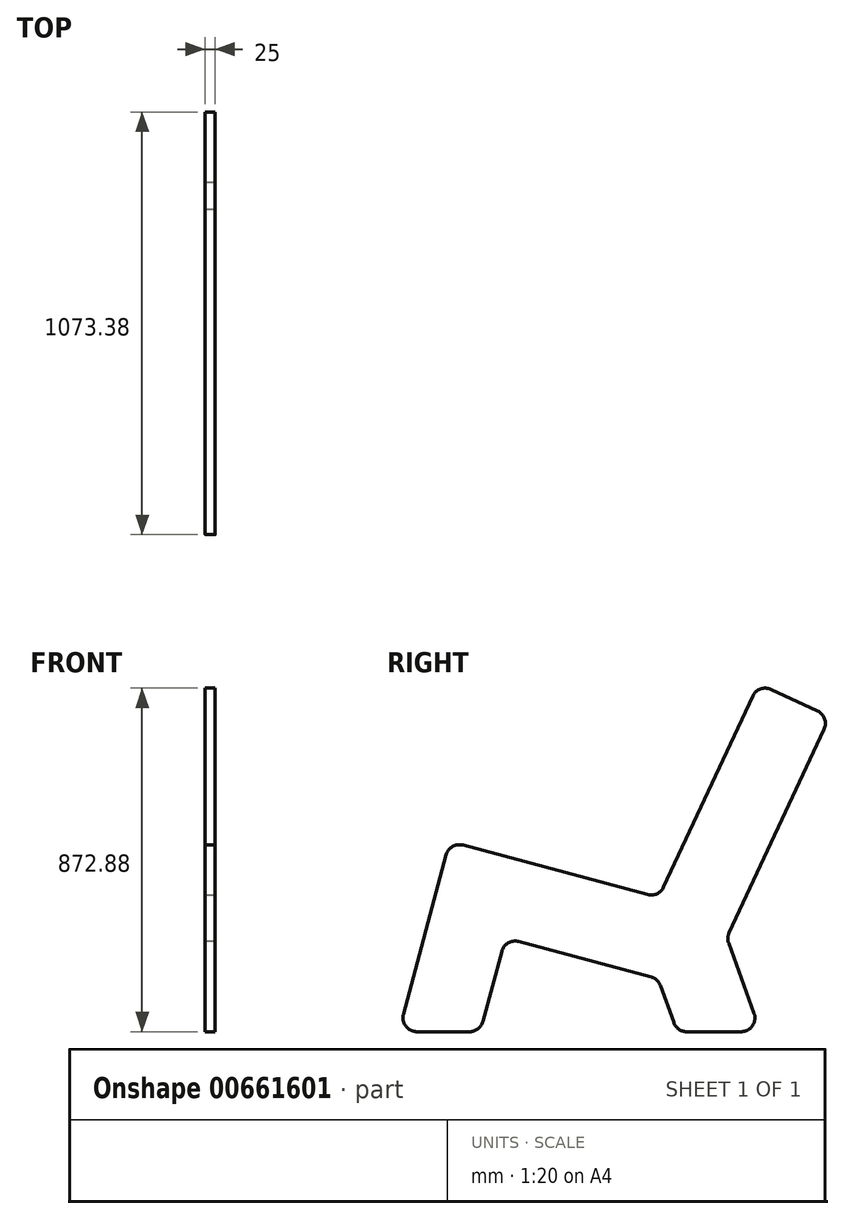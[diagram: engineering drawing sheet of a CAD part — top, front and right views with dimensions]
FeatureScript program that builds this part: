
annotation { "Feature Type Name" : "Feature", "Feature Type Description" : "" }
export const myFeature = defineFeature(function(context is Context, id is Id, definition is map)
    precondition{}
    {
        {
            var Q0;
            Q0=qCreatedBy(makeId("Right.planeOp"),FACE);
            cPlane(context, id + "F0", {"entities" : qUnion([Q0]), "cplaneType" : CPlaneType.OFFSET, "offset" : 400 * mm, "oppositeDirection" : true, "width" : 150 * mm, "height" : 150 * mm});
        }
        {
            var Q0;
            Q0=qCreatedBy(id+"F0.planeOp",FACE);
            var sketch = newSketch(context, id + "F1", { "sketchPlane" : qUnion([Q0])});
            skLineSegment(sketch, "E0", {"start": v(0, 0) * mm, "end": v(129.4, 482.96) * mm});
            skLineSegment(sketch, "E1", {"start": v(129.4, 482.96) * mm, "end": v(660.67, 340.61) * mm});
            skLineSegment(sketch, "E2", {"start": v(660.67, 340.61) * mm, "end": v(914.24, 884.4) * mm});
            skLineSegment(sketch, "E3", {"start": v(914.24, 884.4) * mm, "end": v(1095.5, 799.87) * mm});
            skLineSegment(sketch, "E4", {"start": v(1095.5, 799.87) * mm, "end": v(833.37, 237.72) * mm});
            skLineSegment(sketch, "E5", {"start": v(0, 0) * mm, "end": v(207.06, 0) * mm});
            skLineSegment(sketch, "E6", {"start": v(207.06, 0) * mm, "end": v(270.83, 238.01) * mm});
            skLineSegment(sketch, "E7", {"start": v(270.83, 238.01) * mm, "end": v(658.2, 134.22) * mm});
            skLineSegment(sketch, "E8", {"start": v(658.2, 134.22) * mm, "end": v(707.06, 0) * mm});
            skLineSegment(sketch, "E9", {"start": v(707.06, 0) * mm, "end": v(919.9, 0) * mm});
            skLineSegment(sketch, "E10", {"start": v(919.9, 0) * mm, "end": v(833.37, 237.72) * mm});
            skSolve(sketch);
        }
        {
            var Q0;
            Q0=makeQuery(id+"F1.imprint","IMPRINT",FACE,{"disambiguationData":[TD([[makeQuery(id+"F1.imprint","IMPRINT",EDGE,{"derivedFrom":sQuery(id+"F1.wireOp",EDGE,"E0")}),-1.0]])]});
            extrude(context, id + "F2", {"entities" : qUnion([Q0]), "depth" : 25 * mm, "offsetDistance" : 25 * mm});
        }
        {
            var Q0;
            Q0=makeQuery(id+"F2.opExtrude","SWEPT_EDGE",EDGE,{"disambiguationData":[OSD([sQuery(id+"F1.wireOp",EDGE,"E0"),sQuery(id+"F1.wireOp",EDGE,"E1")])]});
            var Q1;
            Q1=makeQuery(id+"F2.opExtrude","SWEPT_EDGE",EDGE,{"disambiguationData":[OSD([sQuery(id+"F1.wireOp",EDGE,"E1"),sQuery(id+"F1.wireOp",EDGE,"E2")])]});
            var Q2;
            Q2=makeQuery(id+"F2.opExtrude","SWEPT_EDGE",EDGE,{"disambiguationData":[OSD([sQuery(id+"F1.wireOp",EDGE,"E2"),sQuery(id+"F1.wireOp",EDGE,"E3")])]});
            var Q3;
            Q3=makeQuery(id+"F2.opExtrude","SWEPT_EDGE",EDGE,{"disambiguationData":[OSD([sQuery(id+"F1.wireOp",EDGE,"E3"),sQuery(id+"F1.wireOp",EDGE,"E4")])]});
            var Q4;
            Q4=makeQuery(id+"F2.opExtrude","SWEPT_EDGE",EDGE,{"disambiguationData":[OSD([sQuery(id+"F1.wireOp",EDGE,"E6"),sQuery(id+"F1.wireOp",EDGE,"E7")])]});
            var Q5;
            Q5=makeQuery(id+"F2.opExtrude","SWEPT_EDGE",EDGE,{"disambiguationData":[OSD([sQuery(id+"F1.wireOp",EDGE,"E7"),sQuery(id+"F1.wireOp",EDGE,"E8")])]});
            var Q6;
            Q6=makeQuery(id+"F2.opExtrude","SWEPT_EDGE",EDGE,{"disambiguationData":[OSD([sQuery(id+"F1.wireOp",EDGE,"E0"),sQuery(id+"F1.wireOp",EDGE,"E5")])]});
            var Q7;
            Q7=makeQuery(id+"F2.opExtrude","SWEPT_EDGE",EDGE,{"disambiguationData":[OSD([sQuery(id+"F1.wireOp",EDGE,"E5"),sQuery(id+"F1.wireOp",EDGE,"E6")])]});
            var Q8;
            Q8=makeQuery(id+"F2.opExtrude","SWEPT_EDGE",EDGE,{"disambiguationData":[OSD([sQuery(id+"F1.wireOp",EDGE,"E8"),sQuery(id+"F1.wireOp",EDGE,"E9")])]});
            var Q9;
            Q9=makeQuery(id+"F2.opExtrude","SWEPT_EDGE",EDGE,{"disambiguationData":[OSD([sQuery(id+"F1.wireOp",EDGE,"E9"),sQuery(id+"F1.wireOp",EDGE,"E10")])]});
            var Q10;
            Q10=makeQuery(id+"F2.opExtrude","SWEPT_EDGE",EDGE,{"disambiguationData":[OSD([sQuery(id+"F1.wireOp",EDGE,"E4"),sQuery(id+"F1.wireOp",EDGE,"E10")])]});
            fillet(context, id + "F3", {"entities" : qUnion([Q0, Q1, Q2, Q3, Q4, Q5, Q6, Q7, Q8, Q9, Q10]), "radius" : 35 * mm, "tangentPropagation" : true, "allowEdgeOverflow" : false});
        }
    });
